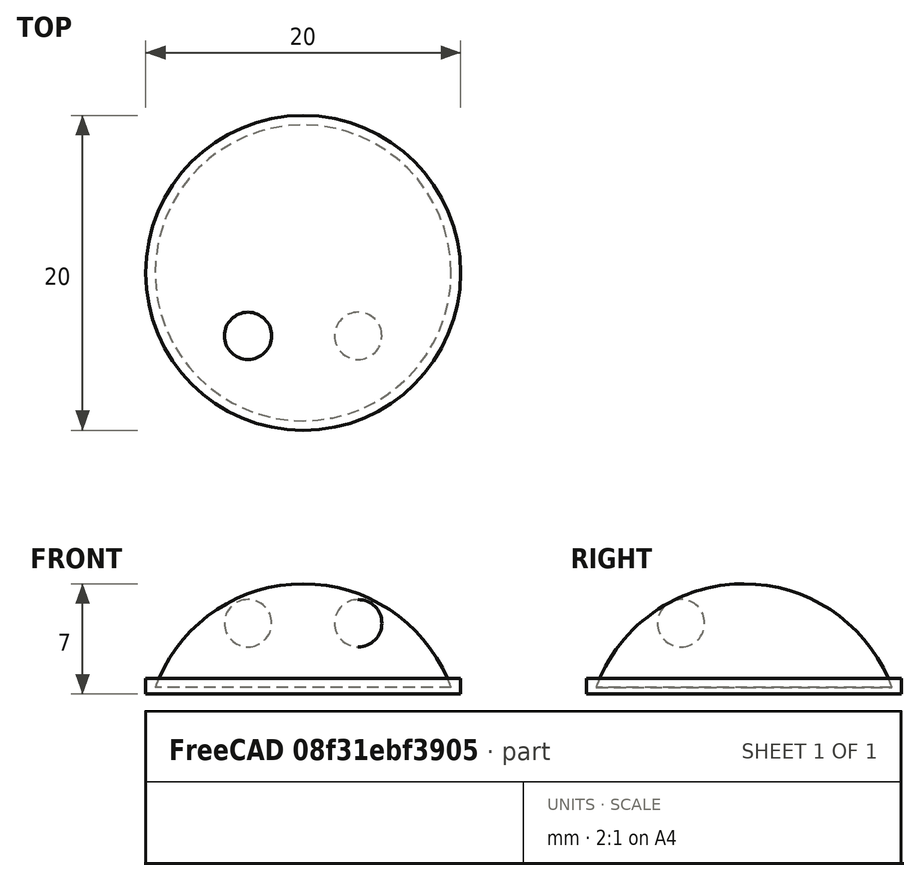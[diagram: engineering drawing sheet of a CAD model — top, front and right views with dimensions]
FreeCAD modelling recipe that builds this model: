
FCSTD DOCUMENT  (FreeCAD 0.21R33771 (Git))
Label: OJT1_T13R01_cap de robot
License: All rights reserved
LicenseURL: http://en.wikipedia.org/wiki/All_rights_reserved
objects: Part::Sphere×3, Part::Cylinder×1
note: 4 computed .brp shape members not serialized (recipe doc carries the construction recipe); baked Part::Feature solids carry a one-line shape summary decoded from their .brp

FEATURE [Part::Cylinder] Cylinder
  Angle = 360
  AttacherType = Attacher::AttachEngine3D
  FirstAngle = 0
  Height = 1
  Radius = 10
  SecondAngle = 0
FEATURE [Part::Sphere] Sphere
  Angle1 = 20
  Angle2 = 90
  Angle3 = 360
  AttacherType = Attacher::AttachEngine3D
  Placement = pos=(0,0,-3) rot=(0,0,1;0rad)
  Radius = 10
FEATURE [Part::Sphere] Sphere001
  Angle1 = -90
  Angle2 = 90
  Angle3 = 360
  AttacherType = Attacher::AttachEngine3D
  Placement = pos=(-3.5,-4,4.5) rot=(0,0,1;0rad)
  Radius = 1.5
FEATURE [Part::Sphere] Sphere002
  Angle1 = -90
  Angle2 = 90
  Angle3 = 360
  AttacherType = Attacher::AttachEngine3D
  Placement = pos=(3.5,-4,4.5) rot=(0,0,1;0rad)
  Radius = 1.5
